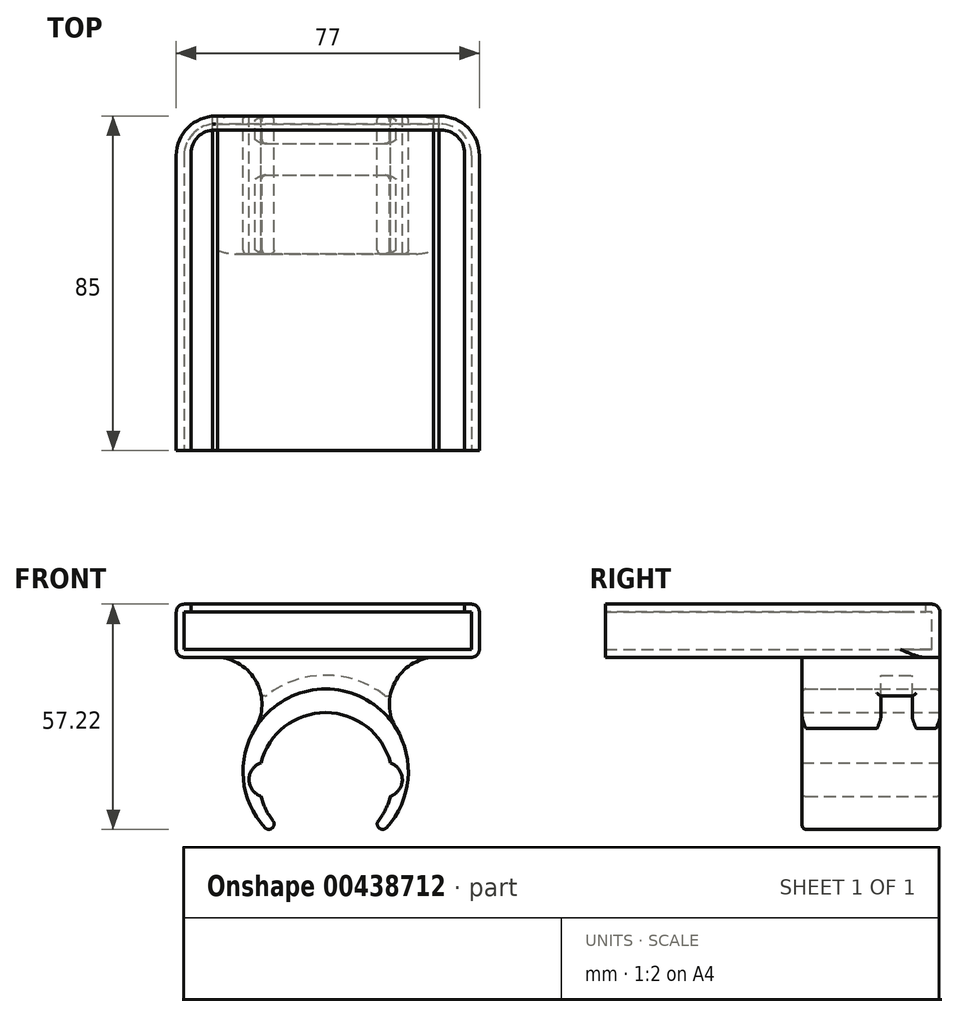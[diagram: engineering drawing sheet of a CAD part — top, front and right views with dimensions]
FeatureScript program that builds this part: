
annotation { "Feature Type Name" : "Feature", "Feature Type Description" : "" }
export const myFeature = defineFeature(function(context is Context, id is Id, definition is map)
    precondition{}
    {
        {
            var Q0;
            Q0=qCreatedBy(makeId("Front.planeOp"),FACE);
            var sketch = newSketch(context, id + "F0", { "sketchPlane" : qUnion([Q0])});
            skArc(sketch, "E0", {"start": v(13.4, -10.47) * mm, "mid": v(15.25, -7.52) * mm, "end": v(16.46, -4.25) * mm});
            skArc(sketch, "E1.0", {"start": v(15.45, -12.22) * mm, "mid": v(0, 23) * mm, "end": v(-15.45, -12.22) * mm});
            skArc(sketch, "E2.filletArc", {"start": v(-15.45, -12.22) * mm, "mid": v(-13.58, -12.34) * mm, "end": v(-13.4, -10.47) * mm});
            skArc(sketch, "E3.filletArc", {"start": v(13.4, -10.47) * mm, "mid": v(13.58, -12.34) * mm, "end": v(15.45, -12.22) * mm});
            skArc(sketch, "E4", {"start": v(-16.46, 4.25) * mm, "mid": v(-19.47, 0) * mm, "end": v(-16.46, -4.25) * mm});
            skArc(sketch, "E5.MirrorC", {"start": v(16.46, 4.25) * mm, "mid": v(19.47, 0) * mm, "end": v(16.46, -4.25) * mm});
            skArc(sketch, "E6.trimOffspring", {"start": v(-16.46, -4.25) * mm, "mid": v(-15.25, -7.52) * mm, "end": v(-13.4, -10.47) * mm});
            skArc(sketch, "E7.trimOffspring", {"start": v(16.46, 4.25) * mm, "mid": v(0, 17) * mm, "end": v(-16.46, 4.25) * mm});
            skSolve(sketch);
        }
        {
            var Q0;
            Q0 = qSketchRegion(id + "F0", true);
            extrude(context, id + "F1", {"entities" : qUnion([Q0]), "depth" : 35 * mm});
        }
        {
            var Q0;
            Q0=qCreatedBy(makeId("Front.planeOp"),FACE);
            var sketch = newSketch(context, id + "F2", { "sketchPlane" : qUnion([Q0])});
            skLineSegment(sketch, "E8.bottom", {"start": v(-35.95, 31.06) * mm, "end": v(37.05, 31.06) * mm});
            skLineSegment(sketch, "E8.top", {"start": v(-37.95, 44.56) * mm, "end": v(39.05, 44.56) * mm});
            skLineSegment(sketch, "E8.left", {"start": v(-37.95, 33.06) * mm, "end": v(-37.95, 44.56) * mm});
            skLineSegment(sketch, "E8.right", {"start": v(39.05, 33.06) * mm, "end": v(39.05, 44.56) * mm});
            skPoint(sketch, "E9.visualSharp", {"position": v(37.05, 31.06) * mm});
            skArc(sketch, "E9.filletArc", {"start": v(37.05, 31.06) * mm, "mid": v(38.46, 31.65) * mm, "end": v(39.05, 33.06) * mm});
            skPoint(sketch, "E10.visualSharp", {"position": v(-35.95, 31.06) * mm});
            skArc(sketch, "E10.filletArc", {"start": v(-37.95, 33.06) * mm, "mid": v(-37.36, 31.65) * mm, "end": v(-35.95, 31.06) * mm});
            skArc(sketch, "E11", {"start": v(-17.9, 12.98) * mm, "mid": v(-17.89, 25.28) * mm, "end": v(-28.75, 31.06) * mm});
            skLineSegment(sketch, "E12", {"start": v(0, 0) * mm, "end": v(0, 42.79) * mm, "construction": true});
            skArc(sketch, "E13.MirrorCS", {"start": v(17.9, 12.98) * mm, "mid": v(17.89, 25.28) * mm, "end": v(28.75, 31.06) * mm});
            skArc(sketch, "E14.0", {"start": v(17.9, 12.98) * mm, "mid": v(0, 23) * mm, "end": v(-17.9, 12.98) * mm});
            skPoint(sketch, "E15.orphan", {"position": v(-15.45, -12.22) * mm});
            skPoint(sketch, "E16.orphan", {"position": v(15.45, -12.22) * mm});
            skSolve(sketch);
        }
        {
            var Q0;
            Q0=makeQuery(id+"F2.imprint","IMPRINT",FACE,{"disambiguationData":[TD([[makeQuery(id+"F2.imprint","IMPRINT",EDGE,{"derivedFrom":sQuery(id+"F2.wireOp",EDGE,"E8.top")}),-1.0]])]});
            extrude(context, id + "F3", {"entities" : qUnion([Q0]), "depth" : 85 * mm});
        }
        {
            var Q0;
            {var subQ5=sQuery(id+"F2.wireOp",EDGE,"E14.0");Q0=makeQuery(id+"F2.imprint","IMPRINT",FACE,{"disambiguationData":[TD([[makeQuery(id+"F2.imprint","IMPRINT",EDGE,{"derivedFrom":subQ5}),-1.0]])]});}
            extrude(context, id + "F4", {"entities" : qUnion([Q0]), "depth" : 35 * mm});
        }
        {
            var Q0;
            Q0=qCreatedBy(makeId("Front.planeOp"),FACE);
            cPlane(context, id + "F5", {"entities" : qUnion([Q0]), "cplaneType" : CPlaneType.OFFSET, "offset" : 7 * mm, "width" : 150 * mm, "height" : 150 * mm});
        }
        {
            var Q0;
            Q0=qCreatedBy(id+"F5.planeOp",FACE);
            var sketch = newSketch(context, id + "F6", { "sketchPlane" : qUnion([Q0])});
            skArc(sketch, "E17.0", {"start": v(15.45, -12.22) * mm, "mid": v(0, 23) * mm, "end": v(-15.45, -12.22) * mm});
            skSolve(sketch);
        }
        {
            var Q0;
            Q0=sQuery(id+"F6.wireOp",VERTEX,"E17.0.end");
            var Q1;
            Q1=sQuery(id+"F6.wireOp",EDGE,"E17.0");
            cPlane(context, id + "F7", {"entities" : qUnion([Q0, Q1]), "cplaneType" : CPlaneType.CURVE_POINT, "offset" : 25 * mm, "width" : 150 * mm, "height" : 150 * mm});
        }
        {
            var Q0;
            Q0=qCreatedBy(id+"F7.planeOp",FACE);
            var sketch = newSketch(context, id + "F8", { "sketchPlane" : qUnion([Q0])});
            skLineSegment(sketch, "E18.bottom", {"start": v(-19.65, 7) * mm, "end": v(-23.15, 7) * mm});
            skLineSegment(sketch, "E18.top", {"start": v(-19.65, 15) * mm, "end": v(-23.15, 15) * mm});
            skLineSegment(sketch, "E18.left", {"start": v(-19.65, 7) * mm, "end": v(-19.65, 15) * mm});
            skLineSegment(sketch, "E18.right", {"start": v(-23.15, 7) * mm, "end": v(-23.15, 15) * mm});
            skLineSegment(sketch, "E19.0.1.0", {"start": v(-19.65, 19.5) * mm, "end": v(-19.65, 27.5) * mm});
            skLineSegment(sketch, "E19.0.1.1", {"start": v(-19.65, 19.5) * mm, "end": v(-23.15, 19.5) * mm});
            skLineSegment(sketch, "E19.0.1.2", {"start": v(-23.15, 19.5) * mm, "end": v(-23.15, 27.5) * mm});
            skLineSegment(sketch, "E19.0.1.3", {"start": v(-19.65, 27.5) * mm, "end": v(-23.15, 27.5) * mm});
            skLineSegment(sketch, "E19.1.1.0", {"start": v(-19.65, 19.5) * mm, "end": v(-19.65, 27.5) * mm});
            skLineSegment(sketch, "E19.1.1.1", {"start": v(-19.65, 19.5) * mm, "end": v(-23.15, 19.5) * mm});
            skLineSegment(sketch, "E19.1.1.2", {"start": v(-23.15, 19.5) * mm, "end": v(-23.15, 27.5) * mm});
            skLineSegment(sketch, "E19.1.1.3", {"start": v(-19.65, 27.5) * mm, "end": v(-23.15, 27.5) * mm});
            skLineSegment(sketch, "E19.2.1.0", {"start": v(-19.65, 19.5) * mm, "end": v(-19.65, 27.5) * mm});
            skLineSegment(sketch, "E19.2.1.1", {"start": v(-19.65, 19.5) * mm, "end": v(-23.15, 19.5) * mm});
            skLineSegment(sketch, "E19.2.1.2", {"start": v(-23.15, 19.5) * mm, "end": v(-23.15, 27.5) * mm});
            skLineSegment(sketch, "E19.2.1.3", {"start": v(-19.65, 27.5) * mm, "end": v(-23.15, 27.5) * mm});
            skLineSegment(sketch, "E19.direction1", {"start": v(-19.65, 7) * mm, "end": v(-19.65, 7) * mm});
            skLineSegment(sketch, "E19.direction2", {"start": v(-19.65, 7) * mm, "end": v(-19.65, 19.5) * mm, "construction": true});
            skSolve(sketch);
        }
        {
            var Q0;
            Q0=makeQuery(id+"F8.imprint","IMPRINT",FACE,{"disambiguationData":[TD([[makeQuery(id+"F8.imprint","IMPRINT",EDGE,{"derivedFrom":sQuery(id+"F8.wireOp",EDGE,"E18.left")}),1.0]])]});
            var Q1;
            Q1=makeQuery(id+"F8.imprint","IMPRINT",FACE,{"disambiguationData":[TD([[makeQuery(id+"F8.imprint","IMPRINT",EDGE,{"derivedFrom":sQuery(id+"F8.wireOp",EDGE,"E19.2.1.0")}),1.0]])]});
            var Q2;
            Q2=sQuery(id+"F6.wireOp",EDGE,"E17.0");
            sweep(context, id + "F9", {"operationType" : NewBodyOperationType.REMOVE, "profiles" : qUnion([Q0, Q1]), "path" : qUnion([Q2])});
        }
        {
            var Q0;
            Q0=makeQuery(id+"F3.opExtrude","CAP_EDGE",EDGE,{"disambiguationData":[OSD([sQuery(id+"F2.wireOp",EDGE,"E8.right")])],"isStart":true});
            var Q1;
            Q1=makeQuery(id+"F3.opExtrude","CAP_EDGE",EDGE,{"disambiguationData":[OSD([sQuery(id+"F2.wireOp",EDGE,"E8.left")])],"isStart":true});
            fillet(context, id + "F10", {"entities" : qUnion([Q0, Q1]), "radius" : 10 * mm, "allowEdgeOverflow" : false});
        }
        {
            var Q0;
            Q0=makeQuery(id+"F3.opExtrude","SWEPT_EDGE",EDGE,{"disambiguationData":[OSD([sQuery(id+"F2.wireOp",EDGE,"E8.top"),sQuery(id+"F2.wireOp",EDGE,"E8.left")])]});
            fillet(context, id + "F11", {"entities" : qUnion([Q0]), "radius" : 2 * mm, "tangentPropagation" : true, "allowEdgeOverflow" : false});
        }
        {
            var Q0;
            Q0=makeQuery(id+"F3.opExtrude","CAP_FACE",FACE,{"disambiguationData":[OSD([sQuery(id+"F2.wireOp",EDGE,"E8.bottom"),sQuery(id+"F2.wireOp",EDGE,"E8.top"),sQuery(id+"F2.wireOp",EDGE,"E8.left"),sQuery(id+"F2.wireOp",EDGE,"E8.right"),sQuery(id+"F2.wireOp",EDGE,"E9.filletArc"),sQuery(id+"F2.wireOp",EDGE,"E10.filletArc"),sQuery(id+"F2.wireOp",EDGE,"E11"),sQuery(id+"F2.wireOp",EDGE,"E13.MirrorCS")])],"isStart":false});
            shell(context, id + "F12", {"entities" : qUnion([Q0]), "thickness" : 2 * mm});
        }
        {
            var Q0;
            Q0=makeQuery(id+"F3.opExtrude","SWEPT_FACE",FACE,{"disambiguationData":[OSD([sQuery(id+"F2.wireOp",EDGE,"E8.top")])]});
            var sketch = newSketch(context, id + "F13", { "sketchPlane" : qUnion([Q0])});
            skLineSegment(sketch, "E20.bottom", {"start": v(-34.2, -87.96) * mm, "end": v(35.3, -87.96) * mm});
            skLineSegment(sketch, "E20.top", {"start": v(-28.2, -3.5) * mm, "end": v(29.3, -3.5) * mm});
            skLineSegment(sketch, "E20.left", {"start": v(-34.2, -87.96) * mm, "end": v(-34.2, -9.5) * mm});
            skLineSegment(sketch, "E20.right", {"start": v(35.3, -87.96) * mm, "end": v(35.3, -9.5) * mm});
            skPoint(sketch, "E21.visualSharp", {"position": v(-35.3, -2) * mm});
            skArc(sketch, "E21.filletArc", {"start": v(-28.2, -3.5) * mm, "mid": v(-32.44, -5.26) * mm, "end": v(-34.2, -9.5) * mm});
            skPoint(sketch, "E22.visualSharp", {"position": v(34.2, -2) * mm});
            skArc(sketch, "E22.filletArc", {"start": v(35.3, -9.5) * mm, "mid": v(33.54, -5.26) * mm, "end": v(29.3, -3.5) * mm});
            skSolve(sketch);
        }
        {
            var Q0;
            Q0 = qSketchRegion(id + "F13", true);
            extrude(context, id + "F14", {"entities" : qUnion([Q0]), "operationType" : NewBodyOperationType.REMOVE, "oppositeDirection" : true, "depth" : 3 * mm});
        }
        {
            var Q0;
            Q0=makeQuery(id+"F4.opExtrude","CAP_EDGE",EDGE,{"disambiguationData":[OSD([sQuery(id+"F2.wireOp",EDGE,"E11")])],"isStart":false});
            var Q1;
            Q1=makeQuery(id+"F4.opExtrude","CAP_EDGE",EDGE,{"disambiguationData":[OSD([sQuery(id+"F2.wireOp",EDGE,"E13.MirrorCS")])],"isStart":false});
            var Q2;
            Q2=makeQuery(id+"F1.opExtrude","CAP_EDGE",EDGE,{"disambiguationData":[OSD([sQuery(id+"F0.wireOp",EDGE,"E1.0")])],"isStart":false});
            var Q3;
            Q3=makeQuery(id+"F1.opExtrude","CAP_EDGE",EDGE,{"disambiguationData":[OSD([sQuery(id+"F0.wireOp",EDGE,"E1.0")])],"isStart":true});
            var Q4;
            Q4=makeQuery(id+"F4.opExtrude","CAP_EDGE",EDGE,{"disambiguationData":[OSD([sQuery(id+"F2.wireOp",EDGE,"E13.MirrorCS")])],"isStart":true});
            var Q5;
            Q5=makeQuery(id+"F4.opExtrude","CAP_EDGE",EDGE,{"disambiguationData":[OSD([sQuery(id+"F2.wireOp",EDGE,"E11")])],"isStart":true});
            var Q6;
            Q6=makeQuery(id+"F9.boolean.opBoolean","INTERSECT",EDGE,{"derivedFrom":[makeQuery(id+"F4.opExtrude","SWEPT_FACE",FACE,{"disambiguationData":[OSD([sQuery(id+"F2.wireOp",EDGE,"E11")])]}),makeQuery(id+"F9.opSweep","SWEPT_FACE",FACE,{"disambiguationData":[OSD([sQuery(id+"F6.wireOp",EDGE,"E17.0"),sQuery(id+"F8.wireOp",EDGE,"E18.right")])]})]});
            var Q7;
            Q7=makeQuery(id+"F9.boolean.opBoolean","INTERSECT",EDGE,{"derivedFrom":[makeQuery(id+"F4.opExtrude","SWEPT_FACE",FACE,{"disambiguationData":[OSD([sQuery(id+"F2.wireOp",EDGE,"E11")])]}),makeQuery(id+"F9.opSweep","SWEPT_FACE",FACE,{"disambiguationData":[OSD([sQuery(id+"F6.wireOp",EDGE,"E17.0"),sQuery(id+"F8.wireOp",EDGE,"E18.top")])]})]});
            var Q8;
            Q8=makeQuery(id+"F9.boolean.opBoolean","INTERSECT",EDGE,{"derivedFrom":[makeQuery(id+"F4.opExtrude","SWEPT_FACE",FACE,{"disambiguationData":[OSD([sQuery(id+"F2.wireOp",EDGE,"E11")])]}),makeQuery(id+"F9.opSweep","SWEPT_FACE",FACE,{"disambiguationData":[OSD([sQuery(id+"F6.wireOp",EDGE,"E17.0"),sQuery(id+"F8.wireOp",EDGE,"E18.bottom")])]})]});
            var Q9;
            Q9=makeQuery(id+"F9.boolean.opBoolean","INTERSECT",EDGE,{"derivedFrom":[makeQuery(id+"F4.opExtrude","SWEPT_FACE",FACE,{"disambiguationData":[OSD([sQuery(id+"F2.wireOp",EDGE,"E11")])]}),makeQuery(id+"F9.opSweep","SWEPT_FACE",FACE,{"disambiguationData":[OSD([sQuery(id+"F6.wireOp",EDGE,"E17.0"),sQuery(id+"F8.wireOp",EDGE,"E19.2.1.3")])]})]});
            var Q10;
            Q10=makeQuery(id+"F9.boolean.opBoolean","INTERSECT",EDGE,{"derivedFrom":[makeQuery(id+"F4.opExtrude","SWEPT_FACE",FACE,{"disambiguationData":[OSD([sQuery(id+"F2.wireOp",EDGE,"E11")])]}),makeQuery(id+"F9.opSweep","SWEPT_FACE",FACE,{"disambiguationData":[OSD([sQuery(id+"F6.wireOp",EDGE,"E17.0"),sQuery(id+"F8.wireOp",EDGE,"E19.2.1.1")])]})]});
            var Q11;
            Q11=makeQuery(id+"F9.boolean.opBoolean","INTERSECT",EDGE,{"derivedFrom":[makeQuery(id+"F4.opExtrude","SWEPT_FACE",FACE,{"disambiguationData":[OSD([sQuery(id+"F2.wireOp",EDGE,"E11")])]}),makeQuery(id+"F9.opSweep","SWEPT_FACE",FACE,{"disambiguationData":[OSD([sQuery(id+"F6.wireOp",EDGE,"E17.0"),sQuery(id+"F8.wireOp",EDGE,"E19.2.1.2")])]})]});
            var Q12;
            Q12=makeQuery(id+"F9.boolean.opBoolean","INTERSECT",EDGE,{"derivedFrom":[makeQuery(id+"F4.opExtrude","SWEPT_FACE",FACE,{"disambiguationData":[OSD([sQuery(id+"F2.wireOp",EDGE,"E13.MirrorCS")])]}),makeQuery(id+"F9.opSweep","SWEPT_FACE",FACE,{"disambiguationData":[OSD([sQuery(id+"F6.wireOp",EDGE,"E17.0"),sQuery(id+"F8.wireOp",EDGE,"E18.right")])]})]});
            var Q13;
            Q13=makeQuery(id+"F9.boolean.opBoolean","INTERSECT",EDGE,{"derivedFrom":[makeQuery(id+"F4.opExtrude","SWEPT_FACE",FACE,{"disambiguationData":[OSD([sQuery(id+"F2.wireOp",EDGE,"E13.MirrorCS")])]}),makeQuery(id+"F9.opSweep","SWEPT_FACE",FACE,{"disambiguationData":[OSD([sQuery(id+"F6.wireOp",EDGE,"E17.0"),sQuery(id+"F8.wireOp",EDGE,"E19.2.1.2")])]})]});
            var Q14;
            Q14=makeQuery(id+"F9.boolean.opBoolean","INTERSECT",EDGE,{"derivedFrom":[makeQuery(id+"F4.opExtrude","SWEPT_FACE",FACE,{"disambiguationData":[OSD([sQuery(id+"F2.wireOp",EDGE,"E13.MirrorCS")])]}),makeQuery(id+"F9.opSweep","SWEPT_FACE",FACE,{"disambiguationData":[OSD([sQuery(id+"F6.wireOp",EDGE,"E17.0"),sQuery(id+"F8.wireOp",EDGE,"E19.2.1.1")])]})]});
            var Q15;
            Q15=makeQuery(id+"F9.boolean.opBoolean","INTERSECT",EDGE,{"derivedFrom":[makeQuery(id+"F4.opExtrude","SWEPT_FACE",FACE,{"disambiguationData":[OSD([sQuery(id+"F2.wireOp",EDGE,"E13.MirrorCS")])]}),makeQuery(id+"F9.opSweep","SWEPT_FACE",FACE,{"disambiguationData":[OSD([sQuery(id+"F6.wireOp",EDGE,"E17.0"),sQuery(id+"F8.wireOp",EDGE,"E18.top")])]})]});
            var Q16;
            Q16=makeQuery(id+"F9.boolean.opBoolean","INTERSECT",EDGE,{"derivedFrom":[makeQuery(id+"F4.opExtrude","SWEPT_FACE",FACE,{"disambiguationData":[OSD([sQuery(id+"F2.wireOp",EDGE,"E13.MirrorCS")])]}),makeQuery(id+"F9.opSweep","SWEPT_FACE",FACE,{"disambiguationData":[OSD([sQuery(id+"F6.wireOp",EDGE,"E17.0"),sQuery(id+"F8.wireOp",EDGE,"E18.bottom")])]})]});
            var Q17;
            Q17=makeQuery(id+"F9.boolean.opBoolean","INTERSECT",EDGE,{"derivedFrom":[makeQuery(id+"F4.opExtrude","SWEPT_FACE",FACE,{"disambiguationData":[OSD([sQuery(id+"F2.wireOp",EDGE,"E13.MirrorCS")])]}),makeQuery(id+"F9.opSweep","SWEPT_FACE",FACE,{"disambiguationData":[OSD([sQuery(id+"F6.wireOp",EDGE,"E17.0"),sQuery(id+"F8.wireOp",EDGE,"E19.2.1.3")])]})]});
            fillet(context, id + "F15", {"entities" : qUnion([Q0, Q1, Q2, Q3, Q4, Q5, Q6, Q7, Q8, Q9, Q10, Q11, Q12, Q13, Q14, Q15, Q16, Q17]), "radius" : 1 * mm, "tangentPropagation" : true, "allowEdgeOverflow" : false});
        }
    });
